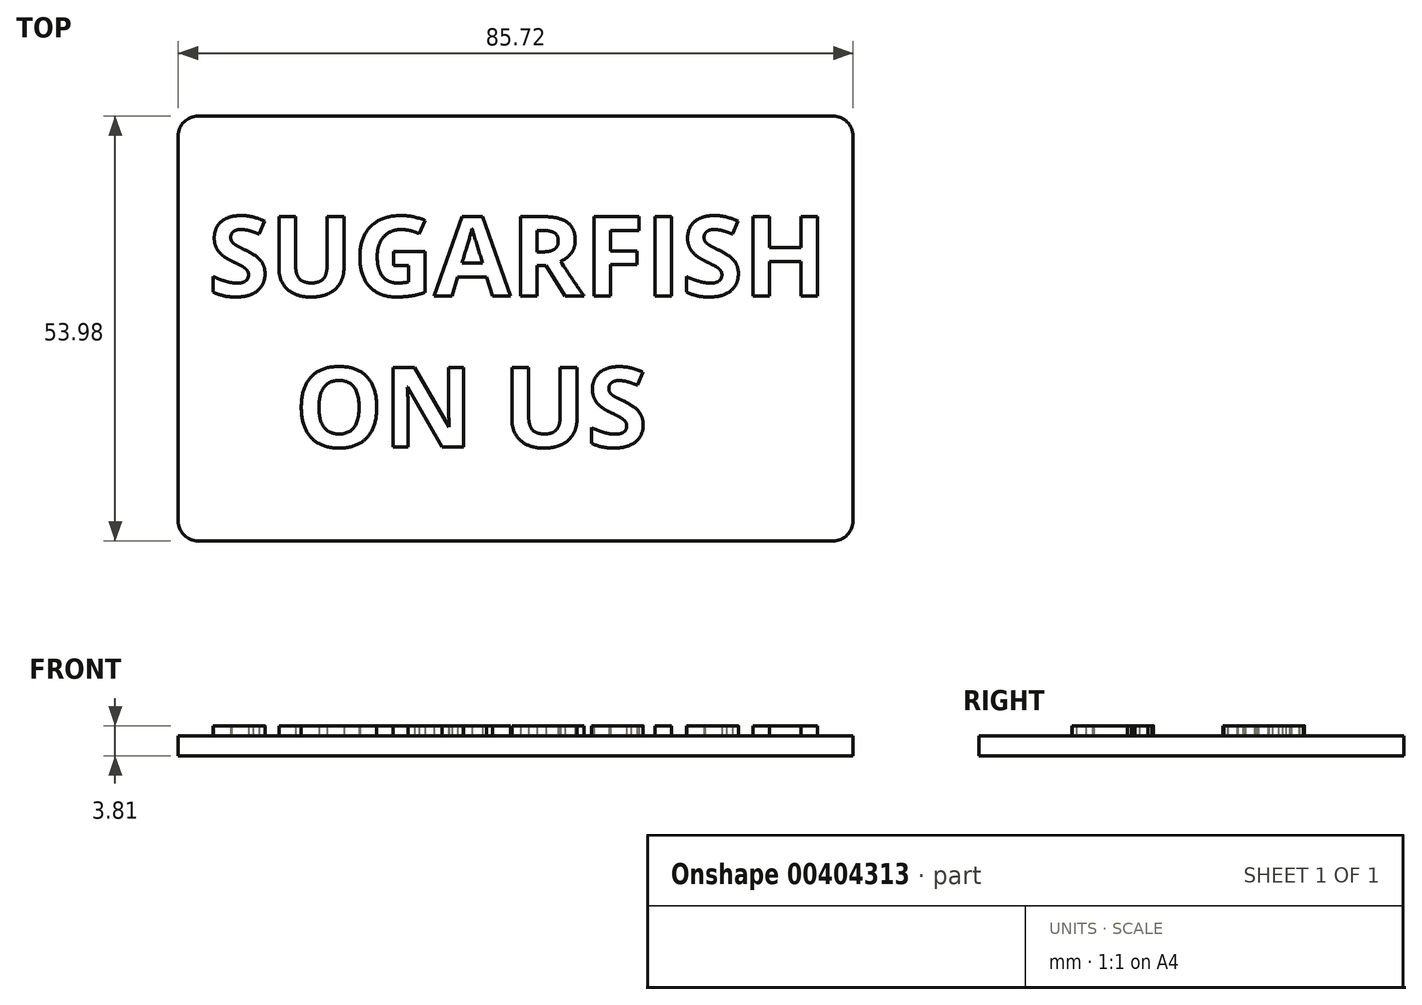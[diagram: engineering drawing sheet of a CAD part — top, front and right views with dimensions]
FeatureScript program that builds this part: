
annotation { "Feature Type Name" : "Feature", "Feature Type Description" : "" }
export const myFeature = defineFeature(function(context is Context, id is Id, definition is map)
    precondition{}
    {
        {
            var Q0;
            Q0=qCreatedBy(makeId("Top.planeOp"),FACE);
            var sketch = newSketch(context, id + "F0", { "sketchPlane" : qUnion([Q0])});
            skLineSegment(sketch, "E0.bottom", {"start": v(40.32, 26.99) * mm, "end": v(-40.32, 26.99) * mm});
            skLineSegment(sketch, "E0.top", {"start": v(40.32, -26.99) * mm, "end": v(-40.32, -26.99) * mm});
            skLineSegment(sketch, "E0.left", {"start": v(42.86, 24.45) * mm, "end": v(42.86, -24.45) * mm});
            skLineSegment(sketch, "E0.right", {"start": v(-42.86, 24.45) * mm, "end": v(-42.86, -24.45) * mm});
            skPoint(sketch, "E0.middle", {"position": v(0, 0) * mm});
            skPoint(sketch, "E1.visualSharp", {"position": v(42.86, 26.99) * mm});
            skArc(sketch, "E1.filletArc", {"start": v(42.86, 24.45) * mm, "mid": v(42.12, 26.24) * mm, "end": v(40.32, 26.99) * mm});
            skPoint(sketch, "E2.visualSharp", {"position": v(42.86, -26.99) * mm});
            skArc(sketch, "E2.filletArc", {"start": v(40.32, -26.99) * mm, "mid": v(42.12, -26.24) * mm, "end": v(42.86, -24.45) * mm});
            skPoint(sketch, "E3.visualSharp", {"position": v(-42.86, -26.99) * mm});
            skArc(sketch, "E3.filletArc", {"start": v(-42.86, -24.45) * mm, "mid": v(-42.12, -26.24) * mm, "end": v(-40.32, -26.99) * mm});
            skPoint(sketch, "E4.visualSharp", {"position": v(-42.86, 26.99) * mm});
            skArc(sketch, "E4.filletArc", {"start": v(-40.32, 26.99) * mm, "mid": v(-42.12, 26.24) * mm, "end": v(-42.86, 24.45) * mm});
            skSolve(sketch);
        }
        {
            var Q0;
            Q0=makeQuery(id+"F0.imprint","IMPRINT",FACE,{"disambiguationData":[TD([[makeQuery(id+"F0.imprint","IMPRINT",EDGE,{"derivedFrom":sQuery(id+"F0.wireOp",EDGE,"E0.bottom")}),1.0]])]});
            extrude(context, id + "F1", {"entities" : qUnion([Q0]), "depth" : 2.54 * mm});
        }
        {
            var Q0;
            Q0=makeQuery(id+"F1.opExtrude","CAP_FACE",FACE,{"disambiguationData":[OSD([sQuery(id+"F0.wireOp",EDGE,"E0.bottom"),sQuery(id+"F0.wireOp",EDGE,"E0.top"),sQuery(id+"F0.wireOp",EDGE,"E0.left"),sQuery(id+"F0.wireOp",EDGE,"E0.right"),sQuery(id+"F0.wireOp",EDGE,"E1.filletArc"),sQuery(id+"F0.wireOp",EDGE,"E2.filletArc"),sQuery(id+"F0.wireOp",EDGE,"E3.filletArc"),sQuery(id+"F0.wireOp",EDGE,"E4.filletArc")])],"isStart":false});
            var sketch = newSketch(context, id + "F2", { "sketchPlane" : qUnion([Q0])});
            skText(sketch, "E5", { "text": "SUGARFISH \n   ON US", "fontName": "OpenSans-Bold.ttf"});
            const initialGuessF2  = {"E5": [-0.03905, 0.00413, 1, 0, 0.01016]};
            skSetInitialGuess(sketch, initialGuessF2);
            skSolve(sketch);
        }
        {
            var Q0;
            Q0=qSketchRegion(id+"F2",true);
            extrude(context, id + "F3", {"entities" : qUnion([Q0]), "operationType" : NewBodyOperationType.ADD, "depth" : 1.27 * mm});
        }
    });
